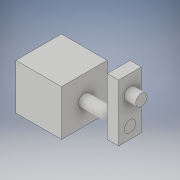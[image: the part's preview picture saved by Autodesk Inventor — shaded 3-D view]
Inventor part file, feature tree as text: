
AUTODESK INVENTOR PART (.ipt)
format: ipt  version: 2019 (Build 230136000, 136)  size: 140,288 bytes
history: native  units: in
note: dims shown in document units (in); Inventor stores cm internally (conversion verified against a paired STEP export)
features: extrude x4, sketch x4
ambient origin geometry x8: Origin, YZ Plane, XZ Plane, XY Plane, X Axis, Y Axis, Z Axis, Center Point
bodies: Solid1 (feature_tree), Solid2 (feature_tree), Solid3 (feature_tree), Solid6 (feature_tree)
feature tree (8):
  extrude  "Extrusion1"  Depth=2.0in
  extrude  "Extrusion2"  Depth=0.5in
  extrude  "Extrusion3"  Depth=1.0in
  extrude  "Extrusion6"  Depth=1.0in
  sketch  "Sketch1"  dims[d0=2.0in d1=2.0in]
  sketch  "Sketch2"  dims[d2=2.0in d3=0.0in d4=0.5in]
  sketch  "Sketch3"  dims[d5=1.0in d6=1.0in]
  sketch  "Sketch5"  dims[d7=2.0in d8=0.0in d9=1.0in d10=2.5in d11=0.5in d12=0.5in d14=0.5in d15=0.0in d16=0.5in d20=0.5in d21=1.0in d22=0.5in d23=0.75in d26=0.5in d27=0.0in]
